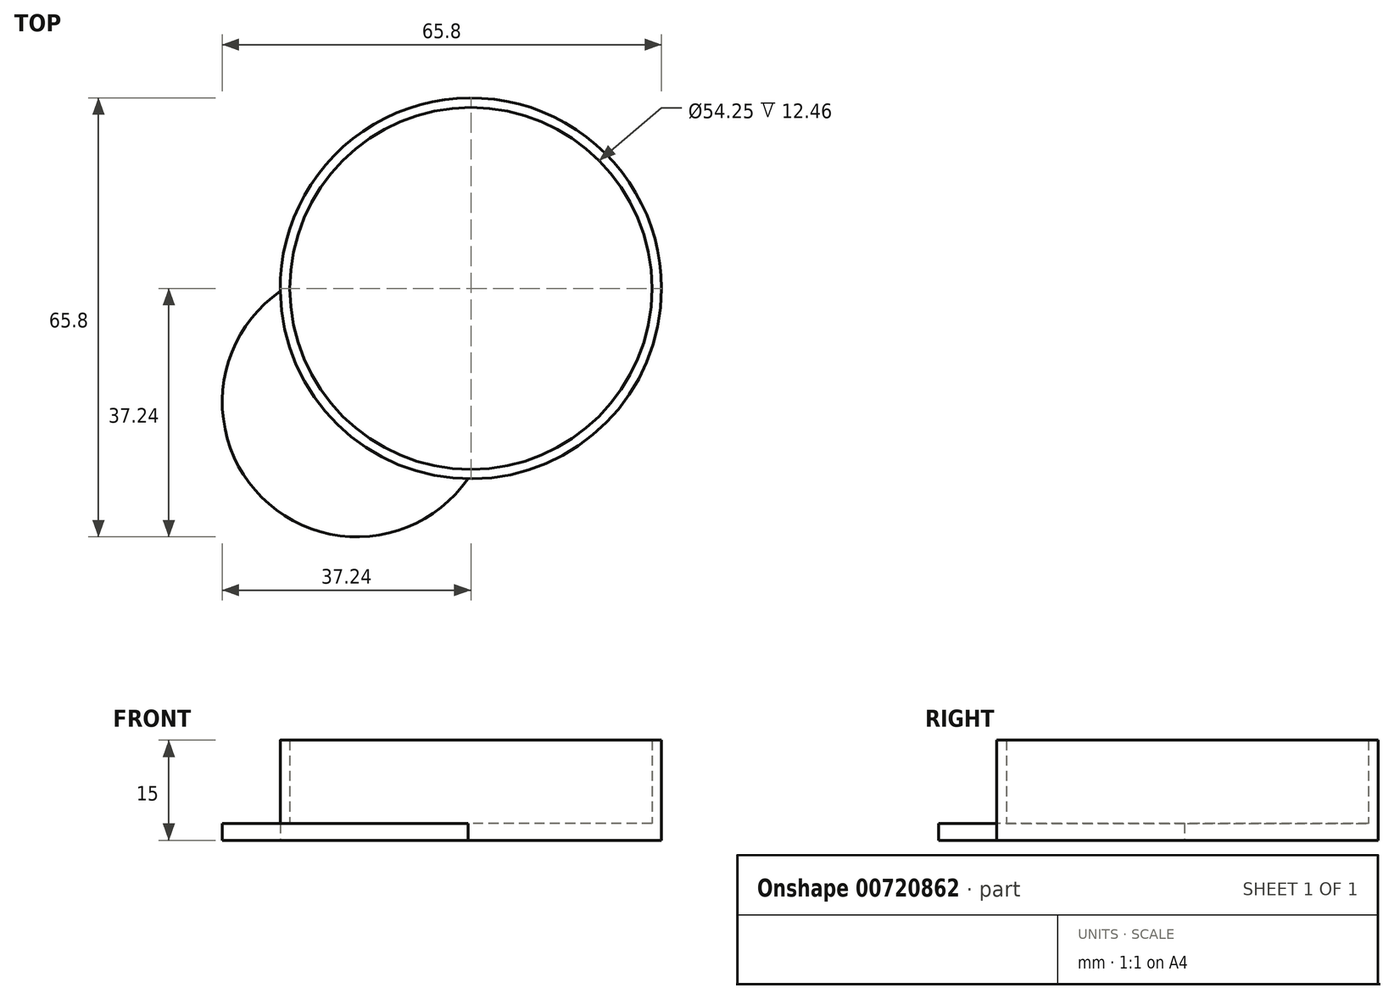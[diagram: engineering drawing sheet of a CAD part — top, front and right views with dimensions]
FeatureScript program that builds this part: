
annotation { "Feature Type Name" : "Feature", "Feature Type Description" : "" }
export const myFeature = defineFeature(function(context is Context, id is Id, definition is map)
    precondition{}
    {
        {
            var Q0;
            Q0=qCreatedBy(makeId("Top.planeOp"),FACE);
            var sketch = newSketch(context, id + "F0", { "sketchPlane" : qUnion([Q0])});
            skCircle(sketch, "E0", {"center": v(0, 0) * mm, "radius": 28.56 * mm});
            skCircle(sketch, "E1", {"center": v(0, 0) * mm, "radius": 27.13 * mm});
            skCircle(sketch, "E2", {"center": v(0, 0) * mm, "radius": 31.4 * mm});
            skCircle(sketch, "E3", {"center": v(0, 0) * mm, "radius": 25.87 * mm});
            skSolve(sketch);
        }
        {
            var Q0;
            Q0=makeQuery(id+"F0.imprint","IMPRINT",FACE,{"disambiguationData":[TD([[makeQuery(id+"F0.imprint","IMPRINT",EDGE,{"derivedFrom":sQuery(id+"F0.wireOp",EDGE,"E0")}),1.0]])]});
            extrude(context, id + "F1", {"entities" : qUnion([Q0]), "depth" : 15 * mm, "offsetDistance" : 25.4 * mm});
        }
        {
            var Q0;
            Q0=qCreatedBy(makeId("Top.planeOp"),FACE);
            var sketch = newSketch(context, id + "F2", { "sketchPlane" : qUnion([Q0])});
            skCircle(sketch, "E4", {"center": v(0, 0) * mm, "radius": 27.91 * mm});
            skArc(sketch, "E5", {"start": v(-27.91, 0) * mm, "mid": v(-31.32, -31.32) * mm, "end": v(0, -27.91) * mm});
            skSolve(sketch);
        }
        {
            var Q0;
            Q0 = qSketchRegion(id + "F2", true);
            extrude(context, id + "F3", {"entities" : qUnion([Q0]), "operationType" : NewBodyOperationType.ADD, "depth" : 2.54 * mm, "offsetDistance" : 25.4 * mm});
        }
    });
